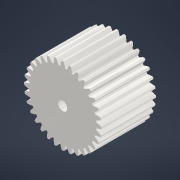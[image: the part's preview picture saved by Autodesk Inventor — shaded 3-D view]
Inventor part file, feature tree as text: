
AUTODESK INVENTOR PART (.ipt)
format: ipt  version: 2021 (Build 250183000, 183)  size: 327,168 bytes
history: native  units: mm (DEFAULTED — no unit token found)
features: plane x3, other x3, sketch x3, extrude x2
ambient origin geometry x8: Origin, YZ Plane, XZ Plane, XY Plane, X Axis, Y Axis, Z Axis, Center Point
bodies: Solid1 (feature_tree)
feature tree (11):
  extrude  "Extrusion1"  Depth=29.967mm TaperAngle=0.0deg
  plane  "Work Plane2"
  plane  "Work Plane8"
  plane  "Work Plane9"
  other  "Spur Gear"
  extrude  "Extrusion2"  Depth=10.0mm TaperAngle=0.0deg
  sketch  "Sketch1"  dims[d0=42.5mm d1=29.967mm d2=0.0mm]
  sketch  "Sketch2"  dims[d3=40.0mm d4=10.0mm d5=0.0mm]
  other  "Srf1"
  sketch  "Sketch3"  dims[d16=85.0mm d17=0.0mm d34=0.981748mm d39=0.0mm d41=0.0mm d43=85.0mm d46=85.0mm d47=0.0mm d48=0.0mm d49=5.0mm d50=41.0mm d51=0.0mm]
  other  "Pitch Diameter"
